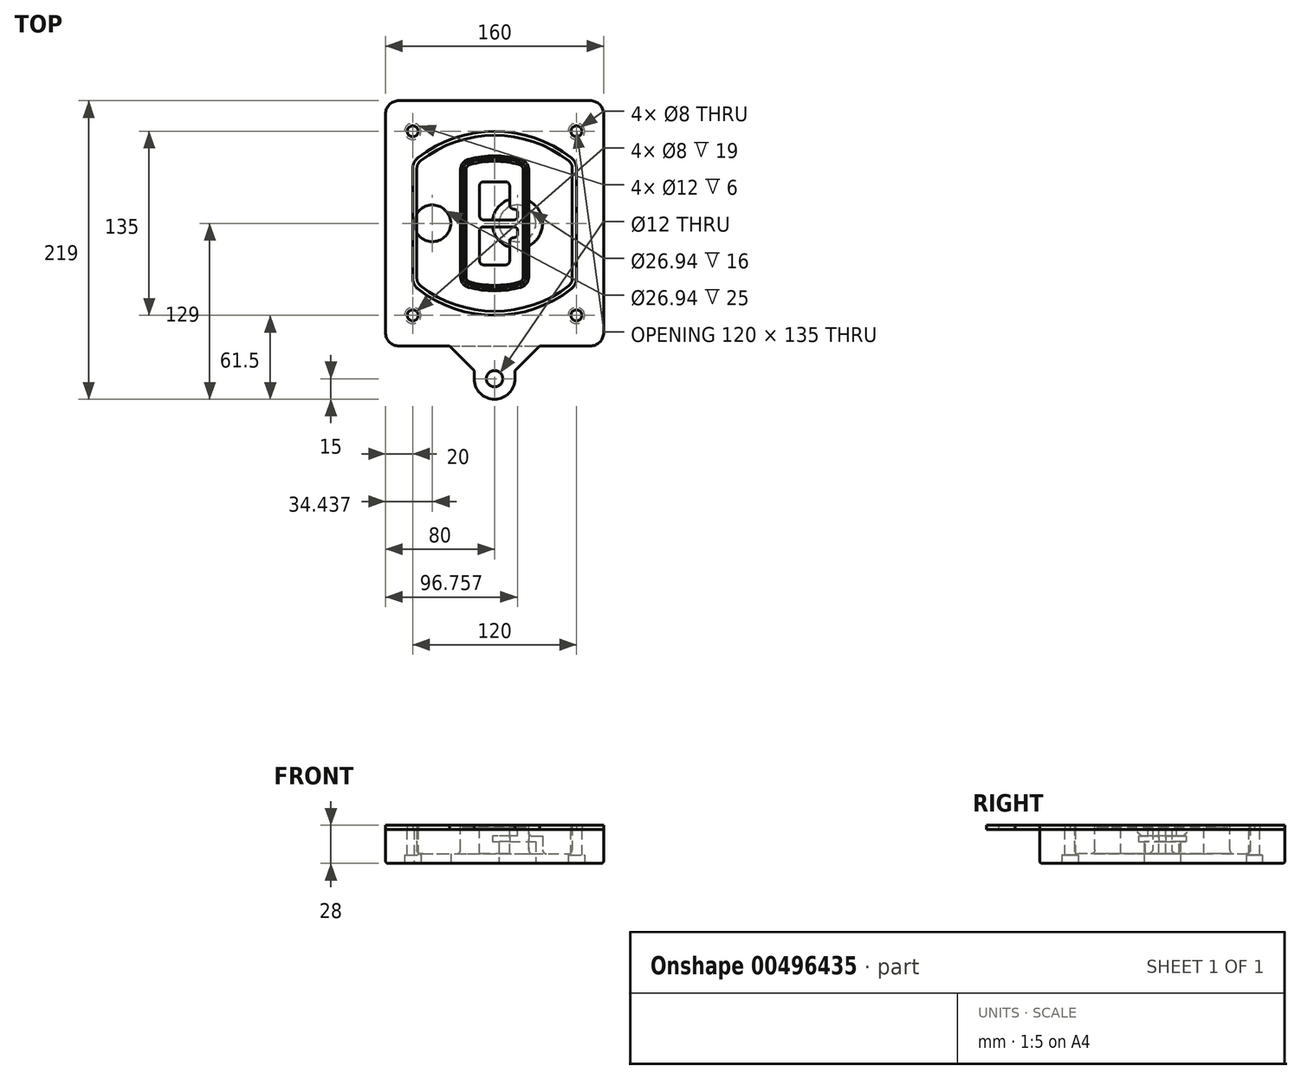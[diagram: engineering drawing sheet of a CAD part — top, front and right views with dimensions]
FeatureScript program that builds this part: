
annotation { "Feature Type Name" : "Feature", "Feature Type Description" : "" }
export const myFeature = defineFeature(function(context is Context, id is Id, definition is map)
    precondition{}
    {
        {
            var Q0;
            Q0=qCreatedBy(makeId("Top.planeOp"),FACE);
            var sketch = newSketch(context, id + "F0", { "sketchPlane" : qUnion([Q0])});
            skPoint(sketch, "E0.rect.middle", {"position": v(0, 0) * mm});
            skLineSegment(sketch, "E1.bottom", {"start": v(-70, -90) * mm, "end": v(70, -90) * mm});
            skLineSegment(sketch, "E1.top", {"start": v(-70, 90) * mm, "end": v(70, 90) * mm});
            skLineSegment(sketch, "E1.left", {"start": v(-80, -80) * mm, "end": v(-80, 80) * mm});
            skLineSegment(sketch, "E1.right", {"start": v(80, -80) * mm, "end": v(80, 80) * mm});
            skLineSegment(sketch, "E2", {"start": v(-80, 90) * mm, "end": v(80, -90) * mm, "construction": true});
            skLineSegment(sketch, "E3", {"start": v(80, 90) * mm, "end": v(-80, -90) * mm, "construction": true});
            skCircle(sketch, "E4", {"center": v(-60, 67.5) * mm, "radius": 4 * mm});
            skCircle(sketch, "E5", {"center": v(60, 67.5) * mm, "radius": 4 * mm});
            skCircle(sketch, "E6", {"center": v(60, -67.5) * mm, "radius": 4 * mm});
            skCircle(sketch, "E7", {"center": v(-60, -67.5) * mm, "radius": 4 * mm});
            skLineSegment(sketch, "E8", {"start": v(-60, 67.5) * mm, "end": v(60, 67.5) * mm, "construction": true});
            skLineSegment(sketch, "E9", {"start": v(60, 67.5) * mm, "end": v(60, -67.5) * mm, "construction": true});
            skLineSegment(sketch, "E10", {"start": v(60, -67.5) * mm, "end": v(-60, -67.5) * mm, "construction": true});
            skLineSegment(sketch, "E11", {"start": v(-60, -67.5) * mm, "end": v(-60, 67.5) * mm, "construction": true});
            skLineSegment(sketch, "E12", {"start": v(-60, 40.3) * mm, "end": v(-60, -40.3) * mm});
            skLineSegment(sketch, "E13", {"start": v(60, 40.3) * mm, "end": v(60, -40.3) * mm});
            skArc(sketch, "E14", {"start": v(56.15, 48.18) * mm, "mid": v(0, 67.5) * mm, "end": v(-56.15, 48.18) * mm});
            skArc(sketch, "E15", {"start": v(-56.15, -48.18) * mm, "mid": v(0, -67.5) * mm, "end": v(56.15, -48.18) * mm});
            skLineSegment(sketch, "E16", {"start": v(-60, 0) * mm, "end": v(60, 0) * mm, "construction": true});
            skPoint(sketch, "E17.visualSharp", {"position": v(-60, -45) * mm});
            skArc(sketch, "E17.filletArc", {"start": v(-60, -40.3) * mm, "mid": v(-58.99, -44.68) * mm, "end": v(-56.15, -48.18) * mm});
            skPoint(sketch, "E18.visualSharp", {"position": v(-60, 45) * mm});
            skArc(sketch, "E18.filletArc", {"start": v(-56.15, 48.18) * mm, "mid": v(-58.99, 44.68) * mm, "end": v(-60, 40.3) * mm});
            skPoint(sketch, "E19.visualSharp", {"position": v(60, 45) * mm});
            skArc(sketch, "E19.filletArc", {"start": v(60, 40.3) * mm, "mid": v(58.99, 44.68) * mm, "end": v(56.15, 48.18) * mm});
            skPoint(sketch, "E20.visualSharp", {"position": v(60, -45) * mm});
            skArc(sketch, "E20.filletArc", {"start": v(56.15, -48.18) * mm, "mid": v(58.99, -44.68) * mm, "end": v(60, -40.3) * mm});
            skPoint(sketch, "E21.visualSharp", {"position": v(-80, 90) * mm});
            skArc(sketch, "E21.filletArc", {"start": v(-70, 90) * mm, "mid": v(-77.07, 87.07) * mm, "end": v(-80, 80) * mm});
            skPoint(sketch, "E22.visualSharp", {"position": v(80, 90) * mm});
            skArc(sketch, "E22.filletArc", {"start": v(80, 80) * mm, "mid": v(77.07, 87.07) * mm, "end": v(70, 90) * mm});
            skPoint(sketch, "E23.visualSharp", {"position": v(80, -90) * mm});
            skArc(sketch, "E23.filletArc", {"start": v(70, -90) * mm, "mid": v(77.07, -87.07) * mm, "end": v(80, -80) * mm});
            skPoint(sketch, "E24.visualSharp", {"position": v(-80, -90) * mm});
            skArc(sketch, "E24.filletArc", {"start": v(-80, -80) * mm, "mid": v(-77.07, -87.07) * mm, "end": v(-70, -90) * mm});
            skArc(sketch, "E25.0", {"start": v(57, 40.3) * mm, "mid": v(56.3, 43.36) * mm, "end": v(54.3, 45.81) * mm});
            skLineSegment(sketch, "E25.1", {"start": v(57, 40.3) * mm, "end": v(57, -40.3) * mm});
            skArc(sketch, "E25.2", {"start": v(54.3, -45.81) * mm, "mid": v(56.3, -43.36) * mm, "end": v(57, -40.3) * mm});
            skArc(sketch, "E25.3", {"start": v(-54.3, -45.81) * mm, "mid": v(0, -64.5) * mm, "end": v(54.3, -45.81) * mm});
            skArc(sketch, "E25.4", {"start": v(-57, -40.3) * mm, "mid": v(-56.3, -43.36) * mm, "end": v(-54.3, -45.81) * mm});
            skArc(sketch, "E25.5", {"start": v(54.3, 45.81) * mm, "mid": v(0, 64.5) * mm, "end": v(-54.3, 45.81) * mm});
            skLineSegment(sketch, "E25.6", {"start": v(-57, 40.3) * mm, "end": v(-57, -40.3) * mm});
            skArc(sketch, "E25.7", {"start": v(-54.3, 45.81) * mm, "mid": v(-56.3, 43.36) * mm, "end": v(-57, 40.3) * mm});
            skArc(sketch, "E26.0", {"start": v(-58.62, 51.33) * mm, "mid": v(-62.58, 46.43) * mm, "end": v(-64, 40.3) * mm});
            skArc(sketch, "E26.1", {"start": v(58.62, 51.33) * mm, "mid": v(0, 71.5) * mm, "end": v(-58.62, 51.33) * mm});
            skArc(sketch, "E26.2", {"start": v(64, 40.3) * mm, "mid": v(62.58, 46.43) * mm, "end": v(58.62, 51.33) * mm});
            skLineSegment(sketch, "E26.3", {"start": v(64, 40.3) * mm, "end": v(64, -40.3) * mm});
            skArc(sketch, "E26.4", {"start": v(58.62, -51.33) * mm, "mid": v(62.58, -46.43) * mm, "end": v(64, -40.3) * mm});
            skLineSegment(sketch, "E26.5", {"start": v(-64, 40.3) * mm, "end": v(-64, -40.3) * mm});
            skArc(sketch, "E26.6", {"start": v(-58.62, -51.33) * mm, "mid": v(0, -71.5) * mm, "end": v(58.62, -51.33) * mm});
            skArc(sketch, "E26.7", {"start": v(-64, -40.3) * mm, "mid": v(-62.58, -46.43) * mm, "end": v(-58.62, -51.33) * mm});
            skSolve(sketch);
        }
        {
            var Q0;
            Q0=makeQuery(id+"F0.imprint","IMPRINT",FACE,{"disambiguationData":[TD([[makeQuery(id+"F0.imprint","IMPRINT",EDGE,{"derivedFrom":sQuery(id+"F0.wireOp",EDGE,"E1.bottom")}),1.0]])]});
            var Q1;
            Q1=makeQuery(id+"F0.imprint","IMPRINT",FACE,{"disambiguationData":[TD([[makeQuery(id+"F0.imprint","IMPRINT",EDGE,{"derivedFrom":sQuery(id+"F0.wireOp",EDGE,"E12")}),1.0]])]});
            var Q2;
            Q2=makeQuery(id+"F0.imprint","IMPRINT",FACE,{"disambiguationData":[TD([[makeQuery(id+"F0.imprint","IMPRINT",EDGE,{"derivedFrom":sQuery(id+"F0.wireOp",EDGE,"E25.0")}),1.0]])]});
            var Q3;
            Q3=makeQuery(id+"F0.imprint","IMPRINT",FACE,{"disambiguationData":[TD([[makeQuery(id+"F0.imprint","IMPRINT",EDGE,{"derivedFrom":sQuery(id+"F0.wireOp",EDGE,"E12")}),-1.0]])]});
            extrude(context, id + "F1", {"entities" : qUnion([Q0, Q1, Q2, Q3]), "oppositeDirection" : true, "depth" : 25 * mm});
        }
        {
            var Q0;
            Q0=makeQuery(id+"F0.imprint","IMPRINT",FACE,{"disambiguationData":[TD([[makeQuery(id+"F0.imprint","IMPRINT",EDGE,{"derivedFrom":sQuery(id+"F0.wireOp",EDGE,"E12")}),1.0]])]});
            extrude(context, id + "F2", {"entities" : qUnion([Q0]), "operationType" : NewBodyOperationType.ADD, "depth" : 3 * mm});
        }
        {
            var Q0;
            Q0=makeQuery(id+"F0.imprint","IMPRINT",FACE,{"disambiguationData":[TD([[makeQuery(id+"F0.imprint","IMPRINT",EDGE,{"derivedFrom":sQuery(id+"F0.wireOp",EDGE,"E25.0")}),1.0]])]});
            extrude(context, id + "F3", {"entities" : qUnion([Q0]), "operationType" : NewBodyOperationType.REMOVE, "oppositeDirection" : true, "depth" : 18 * mm});
        }
        {
            var Q0;
            Q0=makeQuery(id+"F2.opExtrude","CAP_FACE",FACE,{"disambiguationData":[OSD([sQuery(id+"F0.wireOp",EDGE,"E12"),sQuery(id+"F0.wireOp",EDGE,"E13"),sQuery(id+"F0.wireOp",EDGE,"E14"),sQuery(id+"F0.wireOp",EDGE,"E15"),sQuery(id+"F0.wireOp",EDGE,"E17.filletArc"),sQuery(id+"F0.wireOp",EDGE,"E18.filletArc"),sQuery(id+"F0.wireOp",EDGE,"E19.filletArc"),sQuery(id+"F0.wireOp",EDGE,"E20.filletArc"),sQuery(id+"F0.wireOp",EDGE,"E25.0"),sQuery(id+"F0.wireOp",EDGE,"E25.1"),sQuery(id+"F0.wireOp",EDGE,"E25.2"),sQuery(id+"F0.wireOp",EDGE,"E25.3"),sQuery(id+"F0.wireOp",EDGE,"E25.4"),sQuery(id+"F0.wireOp",EDGE,"E25.5"),sQuery(id+"F0.wireOp",EDGE,"E25.6"),sQuery(id+"F0.wireOp",EDGE,"E25.7")])],"isStart":false});
            var sketch = newSketch(context, id + "F4", { "sketchPlane" : qUnion([Q0])});
            skArc(sketch, "E27.0", {"start": v(-19.08, -46.97) * mm, "mid": v(0, -49.5) * mm, "end": v(19.08, -46.97) * mm});
            skArc(sketch, "E28.0", {"start": v(19.08, 46.97) * mm, "mid": v(0, 49.5) * mm, "end": v(-19.08, 46.97) * mm});
            skLineSegment(sketch, "E29", {"start": v(-25, 39.25) * mm, "end": v(-25, -39.25) * mm});
            skLineSegment(sketch, "E30", {"start": v(25, 39.25) * mm, "end": v(25, -39.25) * mm});
            skLineSegment(sketch, "E31", {"start": v(-25, 45.1) * mm, "end": v(25, 45.1) * mm, "construction": true});
            skLineSegment(sketch, "E32", {"start": v(-25, -45.1) * mm, "end": v(25, -45.1) * mm, "construction": true});
            skPoint(sketch, "E33.visualSharp", {"position": v(-25, 45.1) * mm});
            skArc(sketch, "E33.filletArc", {"start": v(-19.08, 46.97) * mm, "mid": v(-23.35, 44.11) * mm, "end": v(-25, 39.25) * mm});
            skPoint(sketch, "E34.visualSharp", {"position": v(25, 45.1) * mm});
            skArc(sketch, "E34.filletArc", {"start": v(25, 39.25) * mm, "mid": v(23.35, 44.11) * mm, "end": v(19.08, 46.97) * mm});
            skPoint(sketch, "E35.visualSharp", {"position": v(25, -45.1) * mm});
            skArc(sketch, "E35.filletArc", {"start": v(19.08, -46.97) * mm, "mid": v(23.35, -44.11) * mm, "end": v(25, -39.25) * mm});
            skPoint(sketch, "E36.visualSharp", {"position": v(-25, -45.1) * mm});
            skArc(sketch, "E36.filletArc", {"start": v(-25, -39.25) * mm, "mid": v(-23.35, -44.11) * mm, "end": v(-19.08, -46.97) * mm});
            skArc(sketch, "E37.0", {"start": v(54.3, 45.81) * mm, "mid": v(0, 64.5) * mm, "end": v(-54.3, 45.81) * mm});
            skArc(sketch, "E37.1", {"start": v(-54.3, 45.81) * mm, "mid": v(-56.3, 43.36) * mm, "end": v(-57, 40.3) * mm});
            skLineSegment(sketch, "E37.2", {"start": v(-57, 40.3) * mm, "end": v(-57, -40.3) * mm});
            skArc(sketch, "E37.3", {"start": v(-57, -40.3) * mm, "mid": v(-56.3, -43.36) * mm, "end": v(-54.3, -45.81) * mm});
            skArc(sketch, "E37.4", {"start": v(-54.3, -45.81) * mm, "mid": v(0, -64.5) * mm, "end": v(54.3, -45.81) * mm});
            skArc(sketch, "E37.5", {"start": v(54.3, -45.81) * mm, "mid": v(56.3, -43.36) * mm, "end": v(57, -40.3) * mm});
            skLineSegment(sketch, "E37.6", {"start": v(57, 40.3) * mm, "end": v(57, -40.3) * mm});
            skArc(sketch, "E37.7", {"start": v(57, 40.3) * mm, "mid": v(56.3, 43.36) * mm, "end": v(54.3, 45.81) * mm});
            skLineSegment(sketch, "E38.0", {"start": v(23, 39.25) * mm, "end": v(23, -39.25) * mm});
            skArc(sketch, "E38.1", {"start": v(18.56, -45.04) * mm, "mid": v(21.76, -42.9) * mm, "end": v(23, -39.25) * mm});
            skArc(sketch, "E38.2", {"start": v(-18.56, -45.04) * mm, "mid": v(0, -47.5) * mm, "end": v(18.56, -45.04) * mm});
            skArc(sketch, "E38.3", {"start": v(-23, -39.25) * mm, "mid": v(-21.76, -42.9) * mm, "end": v(-18.56, -45.04) * mm});
            skLineSegment(sketch, "E38.4", {"start": v(-23, 39.25) * mm, "end": v(-23, -39.25) * mm});
            skArc(sketch, "E38.5", {"start": v(23, 39.25) * mm, "mid": v(21.76, 42.9) * mm, "end": v(18.56, 45.04) * mm});
            skArc(sketch, "E38.6", {"start": v(-18.56, 45.04) * mm, "mid": v(-21.76, 42.9) * mm, "end": v(-23, 39.25) * mm});
            skArc(sketch, "E38.7", {"start": v(18.56, 45.04) * mm, "mid": v(0, 47.5) * mm, "end": v(-18.56, 45.04) * mm});
            skArc(sketch, "E39.0", {"start": v(21, 39.25) * mm, "mid": v(20.18, 41.68) * mm, "end": v(18.04, 43.1) * mm});
            skLineSegment(sketch, "E39.1", {"start": v(21, 39.25) * mm, "end": v(21, -39.25) * mm});
            skArc(sketch, "E39.2", {"start": v(18.04, -43.1) * mm, "mid": v(20.18, -41.68) * mm, "end": v(21, -39.25) * mm});
            skArc(sketch, "E39.3", {"start": v(-18.04, -43.1) * mm, "mid": v(0, -45.5) * mm, "end": v(18.04, -43.1) * mm});
            skArc(sketch, "E39.4", {"start": v(-21, -39.25) * mm, "mid": v(-20.18, -41.68) * mm, "end": v(-18.04, -43.1) * mm});
            skArc(sketch, "E39.5", {"start": v(18.04, 43.1) * mm, "mid": v(0, 45.5) * mm, "end": v(-18.04, 43.1) * mm});
            skLineSegment(sketch, "E39.6", {"start": v(-21, 39.25) * mm, "end": v(-21, -39.25) * mm});
            skArc(sketch, "E39.7", {"start": v(-18.04, 43.1) * mm, "mid": v(-20.18, 41.68) * mm, "end": v(-21, 39.25) * mm});
            skLineSegment(sketch, "E40", {"start": v(-25, 0) * mm, "end": v(25, 0) * mm, "construction": true});
            skLineSegment(sketch, "E41", {"start": v(-11, 5.5) * mm, "end": v(-11, 27.5) * mm});
            skLineSegment(sketch, "E42", {"start": v(-8, 30.5) * mm, "end": v(8, 30.5) * mm});
            skLineSegment(sketch, "E43", {"start": v(11, 27.5) * mm, "end": v(11, 13.5) * mm});
            skLineSegment(sketch, "E44", {"start": v(14, 10.5) * mm, "end": v(14, 10.5) * mm});
            skLineSegment(sketch, "E45", {"start": v(17, 7.5) * mm, "end": v(17, 5.5) * mm});
            skLineSegment(sketch, "E46", {"start": v(14, 2.5) * mm, "end": v(-8, 2.5) * mm});
            skPoint(sketch, "E47.visualSharp", {"position": v(-11, 30.5) * mm});
            skArc(sketch, "E47.filletArc", {"start": v(-8, 30.5) * mm, "mid": v(-10.12, 29.62) * mm, "end": v(-11, 27.5) * mm});
            skPoint(sketch, "E48.visualSharp", {"position": v(11, 30.5) * mm});
            skArc(sketch, "E48.filletArc", {"start": v(11, 27.5) * mm, "mid": v(10.12, 29.62) * mm, "end": v(8, 30.5) * mm});
            skPoint(sketch, "E49.visualSharp", {"position": v(11, 10.5) * mm});
            skArc(sketch, "E49.filletArc", {"start": v(11, 13.5) * mm, "mid": v(11.88, 11.38) * mm, "end": v(14, 10.5) * mm});
            skPoint(sketch, "E50.visualSharp", {"position": v(17, 10.5) * mm});
            skArc(sketch, "E50.filletArc", {"start": v(17, 7.5) * mm, "mid": v(16.12, 9.62) * mm, "end": v(14, 10.5) * mm});
            skPoint(sketch, "E51.visualSharp", {"position": v(17, 2.5) * mm});
            skArc(sketch, "E51.filletArc", {"start": v(14, 2.5) * mm, "mid": v(16.12, 3.38) * mm, "end": v(17, 5.5) * mm});
            skPoint(sketch, "E52.visualSharp", {"position": v(-11, 2.5) * mm});
            skArc(sketch, "E52.filletArc", {"start": v(-11, 5.5) * mm, "mid": v(-10.12, 3.38) * mm, "end": v(-8, 2.5) * mm});
            skLineSegment(sketch, "E53.0.MirrorCS", {"start": v(14, -2.5) * mm, "end": v(-8, -2.5) * mm});
            skArc(sketch, "E54.0.MirrorCS", {"start": v(-11, -5.5) * mm, "mid": v(-10.12, -3.38) * mm, "end": v(-8, -2.5) * mm});
            skLineSegment(sketch, "E55.0.MirrorCS", {"start": v(-11, -5.5) * mm, "end": v(-11, -27.5) * mm});
            skArc(sketch, "E56.0.MirrorCS", {"start": v(-8, -30.5) * mm, "mid": v(-10.12, -29.62) * mm, "end": v(-11, -27.5) * mm});
            skLineSegment(sketch, "E57.0.MirrorCS", {"start": v(-8, -30.5) * mm, "end": v(8, -30.5) * mm});
            skArc(sketch, "E58.0.MirrorCS", {"start": v(11, -27.5) * mm, "mid": v(10.12, -29.62) * mm, "end": v(8, -30.5) * mm});
            skLineSegment(sketch, "E59.0.MirrorCS", {"start": v(11, -27.5) * mm, "end": v(11, -13.5) * mm});
            skArc(sketch, "E60.0.MirrorCS", {"start": v(11, -13.5) * mm, "mid": v(11.88, -11.38) * mm, "end": v(14, -10.5) * mm});
            skArc(sketch, "E61.0.MirrorCS", {"start": v(17, -7.5) * mm, "mid": v(16.12, -9.62) * mm, "end": v(14, -10.5) * mm});
            skLineSegment(sketch, "E62.0.MirrorCS", {"start": v(17, -7.5) * mm, "end": v(17, -5.5) * mm});
            skArc(sketch, "E63.0.MirrorCS", {"start": v(14, -2.5) * mm, "mid": v(16.12, -3.38) * mm, "end": v(17, -5.5) * mm});
            skSolve(sketch);
        }
        {
            var Q0;
            Q0=makeQuery(id+"F4.imprint","IMPRINT",FACE,{"disambiguationData":[TD([[makeQuery(id+"F4.imprint","IMPRINT",EDGE,{"derivedFrom":sQuery(id+"F4.wireOp",EDGE,"E27.0")}),1.0]])]});
            var Q1;
            Q1=makeQuery(id+"F4.imprint","IMPRINT",FACE,{"disambiguationData":[TD([[makeQuery(id+"F4.imprint","IMPRINT",EDGE,{"derivedFrom":sQuery(id+"F4.wireOp",EDGE,"E38.0")}),-1.0]])]});
            var Q2;
            Q2=makeQuery(id+"F4.imprint","IMPRINT",FACE,{"disambiguationData":[TD([[makeQuery(id+"F4.imprint","IMPRINT",EDGE,{"derivedFrom":sQuery(id+"F4.wireOp",EDGE,"E39.0")}),1.0]])]});
            extrude(context, id + "F5", {"entities" : qUnion([Q0, Q1, Q2]), "operationType" : NewBodyOperationType.ADD, "endBound" : BoundingType.UP_TO_NEXT, "oppositeDirection" : true, "depth" : 25 * mm});
        }
        {
            var Q0;
            Q0=makeQuery(id+"F4.imprint","IMPRINT",FACE,{"disambiguationData":[TD([[makeQuery(id+"F4.imprint","IMPRINT",EDGE,{"derivedFrom":sQuery(id+"F4.wireOp",EDGE,"E38.0")}),-1.0]])]});
            extrude(context, id + "F6", {"entities" : qUnion([Q0]), "operationType" : NewBodyOperationType.REMOVE, "oppositeDirection" : true, "depth" : 2 * mm});
        }
        {
            var Q0;
            Q0=makeQuery(id+"F1.opExtrude","CAP_FACE",FACE,{"disambiguationData":[OSD([sQuery(id+"F0.wireOp",EDGE,"E1.bottom"),sQuery(id+"F0.wireOp",EDGE,"E1.top"),sQuery(id+"F0.wireOp",EDGE,"E1.left"),sQuery(id+"F0.wireOp",EDGE,"E1.right"),sQuery(id+"F0.wireOp",EDGE,"E4"),sQuery(id+"F0.wireOp",EDGE,"E5"),sQuery(id+"F0.wireOp",EDGE,"E6"),sQuery(id+"F0.wireOp",EDGE,"E7"),sQuery(id+"F0.wireOp",EDGE,"E21.filletArc"),sQuery(id+"F0.wireOp",EDGE,"E22.filletArc"),sQuery(id+"F0.wireOp",EDGE,"E23.filletArc"),sQuery(id+"F0.wireOp",EDGE,"E24.filletArc")])],"isStart":false});
            var sketch = newSketch(context, id + "F7", { "sketchPlane" : qUnion([Q0])});
            skCircle(sketch, "E64", {"center": v(16.76, 0) * mm, "radius": 13.47 * mm});
            skCircle(sketch, "E65", {"center": v(-45.56, 0) * mm, "radius": 13.47 * mm});
            skLineSegment(sketch, "E66", {"start": v(80, 0) * mm, "end": v(-80, 0) * mm});
            skCircle(sketch, "E67", {"center": v(16.76, 0) * mm, "radius": 18.47 * mm});
            skCircle(sketch, "E68", {"center": v(60, -67.5) * mm, "radius": 6 * mm});
            skCircle(sketch, "E69", {"center": v(-60, -67.5) * mm, "radius": 6 * mm});
            skCircle(sketch, "E70", {"center": v(-60, 67.5) * mm, "radius": 6 * mm});
            skCircle(sketch, "E71", {"center": v(60, 67.5) * mm, "radius": 6 * mm});
            skSolve(sketch);
        }
        {
            var Q0;
            {var subQ1=sQuery(id+"F7.wireOp",EDGE,"E66");var subQ4=sQuery(id+"F7.wireOp",EDGE,"E64");var subQ6=makeQuery(id+"F7.imprint","INTERSECT",VERTEX,{"disambiguationData":[OD(0.0)],"derivedFrom":[subQ4,subQ1]});Q0=makeQuery(id+"F7.imprint","IMPRINT",FACE,{"disambiguationData":[TD([[makeQuery(id+"F7.imprint","IMPRINT",EDGE,{"disambiguationData":[TD([[subQ6,-1.0]])],"derivedFrom":subQ4}),-1.0]])]});}
            var Q1;
            {var subQ0=sQuery(id+"F7.wireOp",EDGE,"E66");var subQ1=sQuery(id+"F7.wireOp",EDGE,"E64");var subQ3=makeQuery(id+"F7.imprint","INTERSECT",VERTEX,{"disambiguationData":[OD(0.0)],"derivedFrom":[subQ1,subQ0]});Q1=makeQuery(id+"F7.imprint","IMPRINT",FACE,{"disambiguationData":[TD([[makeQuery(id+"F7.imprint","IMPRINT",EDGE,{"disambiguationData":[TD([[subQ3,-1.0]])],"derivedFrom":subQ1}),1.0]])]});}
            var Q2;
            {var subQ0=sQuery(id+"F7.wireOp",EDGE,"E66");var subQ1=sQuery(id+"F7.wireOp",EDGE,"E64");var subQ3=makeQuery(id+"F7.imprint","INTERSECT",VERTEX,{"disambiguationData":[OD(0.0)],"derivedFrom":[subQ1,subQ0]});Q2=makeQuery(id+"F7.imprint","IMPRINT",FACE,{"disambiguationData":[TD([[makeQuery(id+"F7.imprint","IMPRINT",EDGE,{"disambiguationData":[TD([[subQ3,1.0]])],"derivedFrom":subQ1}),1.0]])]});}
            var Q3;
            {var subQ1=sQuery(id+"F7.wireOp",EDGE,"E66");var subQ4=sQuery(id+"F7.wireOp",EDGE,"E64");var subQ6=makeQuery(id+"F7.imprint","INTERSECT",VERTEX,{"disambiguationData":[OD(0.0)],"derivedFrom":[subQ4,subQ1]});Q3=makeQuery(id+"F7.imprint","IMPRINT",FACE,{"disambiguationData":[TD([[makeQuery(id+"F7.imprint","IMPRINT",EDGE,{"disambiguationData":[TD([[subQ6,1.0]])],"derivedFrom":subQ4}),-1.0]])]});}
            extrude(context, id + "F8", {"entities" : qUnion([Q0, Q1, Q2, Q3]), "operationType" : NewBodyOperationType.ADD, "oppositeDirection" : true, "depth" : 20 * mm});
        }
        {
            var Q0;
            {var subQ0=sQuery(id+"F7.wireOp",EDGE,"E66");var subQ1=sQuery(id+"F7.wireOp",EDGE,"E64");var subQ3=makeQuery(id+"F7.imprint","INTERSECT",VERTEX,{"disambiguationData":[OD(0.0)],"derivedFrom":[subQ1,subQ0]});Q0=makeQuery(id+"F7.imprint","IMPRINT",FACE,{"disambiguationData":[TD([[makeQuery(id+"F7.imprint","IMPRINT",EDGE,{"disambiguationData":[TD([[subQ3,-1.0]])],"derivedFrom":subQ1}),1.0]])]});}
            var Q1;
            {var subQ0=sQuery(id+"F7.wireOp",EDGE,"E66");var subQ1=sQuery(id+"F7.wireOp",EDGE,"E64");var subQ3=makeQuery(id+"F7.imprint","INTERSECT",VERTEX,{"disambiguationData":[OD(0.0)],"derivedFrom":[subQ1,subQ0]});Q1=makeQuery(id+"F7.imprint","IMPRINT",FACE,{"disambiguationData":[TD([[makeQuery(id+"F7.imprint","IMPRINT",EDGE,{"disambiguationData":[TD([[subQ3,1.0]])],"derivedFrom":subQ1}),1.0]])]});}
            extrude(context, id + "F9", {"entities" : qUnion([Q0, Q1]), "operationType" : NewBodyOperationType.REMOVE, "oppositeDirection" : true, "depth" : 16 * mm});
        }
        {
            var Q0;
            {var subQ0=sQuery(id+"F7.wireOp",EDGE,"E66");var subQ1=sQuery(id+"F7.wireOp",EDGE,"E65");var subQ3=makeQuery(id+"F7.imprint","INTERSECT",VERTEX,{"disambiguationData":[OD(0.0)],"derivedFrom":[subQ1,subQ0]});Q0=makeQuery(id+"F7.imprint","IMPRINT",FACE,{"disambiguationData":[TD([[makeQuery(id+"F7.imprint","IMPRINT",EDGE,{"disambiguationData":[TD([[subQ3,-1.0]])],"derivedFrom":subQ1}),1.0]])]});}
            var Q1;
            {var subQ0=sQuery(id+"F7.wireOp",EDGE,"E66");var subQ1=sQuery(id+"F7.wireOp",EDGE,"E65");var subQ3=makeQuery(id+"F7.imprint","INTERSECT",VERTEX,{"disambiguationData":[OD(0.0)],"derivedFrom":[subQ1,subQ0]});Q1=makeQuery(id+"F7.imprint","IMPRINT",FACE,{"disambiguationData":[TD([[makeQuery(id+"F7.imprint","IMPRINT",EDGE,{"disambiguationData":[TD([[subQ3,1.0]])],"derivedFrom":subQ1}),1.0]])]});}
            extrude(context, id + "F10", {"entities" : qUnion([Q0, Q1]), "operationType" : NewBodyOperationType.REMOVE, "oppositeDirection" : true, "depth" : 25 * mm});
        }
        {
            var Q0;
            Q0=makeQuery(id+"F7.imprint","IMPRINT",FACE,{"disambiguationData":[TD([[makeQuery(id+"F7.imprint","IMPRINT",EDGE,{"derivedFrom":sQuery(id+"F7.wireOp",EDGE,"E68")}),1.0]])]});
            var Q1;
            Q1=makeQuery(id+"F7.imprint","IMPRINT",FACE,{"disambiguationData":[TD([[makeQuery(id+"F7.imprint","IMPRINT",EDGE,{"derivedFrom":makeQuery(id+"F1.opExtrude","CAP_EDGE",EDGE,{"disambiguationData":[OSD([sQuery(id+"F0.wireOp",EDGE,"E5")])],"isStart":false})}),-1.0]])]});
            var Q2;
            Q2=makeQuery(id+"F7.imprint","IMPRINT",FACE,{"disambiguationData":[TD([[makeQuery(id+"F7.imprint","IMPRINT",EDGE,{"derivedFrom":sQuery(id+"F7.wireOp",EDGE,"E69")}),1.0]])]});
            var Q3;
            Q3=makeQuery(id+"F7.imprint","IMPRINT",FACE,{"disambiguationData":[TD([[makeQuery(id+"F7.imprint","IMPRINT",EDGE,{"derivedFrom":makeQuery(id+"F1.opExtrude","CAP_EDGE",EDGE,{"disambiguationData":[OSD([sQuery(id+"F0.wireOp",EDGE,"E4")])],"isStart":false})}),-1.0]])]});
            var Q4;
            Q4=makeQuery(id+"F7.imprint","IMPRINT",FACE,{"disambiguationData":[TD([[makeQuery(id+"F7.imprint","IMPRINT",EDGE,{"derivedFrom":sQuery(id+"F7.wireOp",EDGE,"E70")}),1.0]])]});
            var Q5;
            Q5=makeQuery(id+"F7.imprint","IMPRINT",FACE,{"disambiguationData":[TD([[makeQuery(id+"F7.imprint","IMPRINT",EDGE,{"derivedFrom":makeQuery(id+"F1.opExtrude","CAP_EDGE",EDGE,{"disambiguationData":[OSD([sQuery(id+"F0.wireOp",EDGE,"E7")])],"isStart":false})}),-1.0]])]});
            var Q6;
            Q6=makeQuery(id+"F7.imprint","IMPRINT",FACE,{"disambiguationData":[TD([[makeQuery(id+"F7.imprint","IMPRINT",EDGE,{"derivedFrom":sQuery(id+"F7.wireOp",EDGE,"E71")}),1.0]])]});
            var Q7;
            Q7=makeQuery(id+"F7.imprint","IMPRINT",FACE,{"disambiguationData":[TD([[makeQuery(id+"F7.imprint","IMPRINT",EDGE,{"derivedFrom":makeQuery(id+"F1.opExtrude","CAP_EDGE",EDGE,{"disambiguationData":[OSD([sQuery(id+"F0.wireOp",EDGE,"E6")])],"isStart":false})}),-1.0]])]});
            extrude(context, id + "F11", {"entities" : qUnion([Q0, Q1, Q2, Q3, Q4, Q5, Q6, Q7]), "operationType" : NewBodyOperationType.REMOVE, "oppositeDirection" : true, "depth" : 6 * mm});
        }
        {
            var Q0;
            Q0=makeQuery(id+"F9.boolean.opBoolean","COPY",FACE,{"derivedFrom":makeQuery(id+"F9.opExtrude","CAP_FACE",FACE,{"disambiguationData":[OSD([sQuery(id+"F7.wireOp",EDGE,"E64")])],"isStart":false})});
            var sketch = newSketch(context, id + "F12", { "sketchPlane" : qUnion([Q0])});
            skArc(sketch, "E72.0", {"start": v(11, 17.55) * mm, "mid": v(2.57, 11.82) * mm, "end": v(-1.54, 2.5) * mm});
            skArc(sketch, "E72.1", {"start": v(-1.54, -2.5) * mm, "mid": v(2.57, -11.82) * mm, "end": v(11, -17.55) * mm});
            skLineSegment(sketch, "E73", {"start": v(-1.54, -2.5) * mm, "end": v(14, -2.5) * mm});
            skLineSegment(sketch, "E74.0", {"start": v(14, 2.5) * mm, "end": v(-1.54, 2.5) * mm});
            skArc(sketch, "E74.1", {"start": v(14, 2.5) * mm, "mid": v(16.12, 3.38) * mm, "end": v(17, 5.5) * mm});
            skLineSegment(sketch, "E74.2", {"start": v(17, 7.5) * mm, "end": v(17, 5.5) * mm});
            skArc(sketch, "E74.3", {"start": v(17, 7.5) * mm, "mid": v(16.12, 9.62) * mm, "end": v(14, 10.5) * mm});
            skArc(sketch, "E74.4", {"start": v(11, 13.5) * mm, "mid": v(11.88, 11.38) * mm, "end": v(14, 10.5) * mm});
            skLineSegment(sketch, "E74.5", {"start": v(11, 17.55) * mm, "end": v(11, 13.5) * mm});
            skLineSegment(sketch, "E74.7", {"start": v(14, -2.5) * mm, "end": v(-1.54, -2.5) * mm});
            skArc(sketch, "E74.8", {"start": v(14, -2.5) * mm, "mid": v(16.12, -3.38) * mm, "end": v(17, -5.5) * mm});
            skLineSegment(sketch, "E74.9", {"start": v(17, -7.5) * mm, "end": v(17, -5.5) * mm});
            skArc(sketch, "E74.10", {"start": v(17, -7.5) * mm, "mid": v(16.12, -9.62) * mm, "end": v(14, -10.5) * mm});
            skArc(sketch, "E74.11", {"start": v(11, -13.5) * mm, "mid": v(11.88, -11.38) * mm, "end": v(14, -10.5) * mm});
            skLineSegment(sketch, "E74.12", {"start": v(11, -17.55) * mm, "end": v(11, -13.5) * mm});
            skPoint(sketch, "E75.orphan", {"position": v(11, -27.5) * mm});
            skPoint(sketch, "E76.orphan", {"position": v(-8, -2.5) * mm});
            skPoint(sketch, "E77.orphan", {"position": v(-8, 2.5) * mm});
            skPoint(sketch, "E78.orphan", {"position": v(11, 27.5) * mm});
            skSolve(sketch);
        }
        {
            var Q0;
            {var subQ7=sQuery(id+"F12.wireOp",EDGE,"E72.0");var subQ14=sQuery(id+"F12.wireOp",EDGE,"E72.1");var subQ16=sQuery(id+"F12.wireOp",EDGE,"E74.1");var subQ18=sQuery(id+"F12.wireOp",EDGE,"E74.8");Q0=qUnion([makeQuery(id+"F12.imprint","IMPRINT",FACE,{"disambiguationData":[TD([[makeQuery(id+"F12.imprint","IMPRINT",EDGE,{"derivedFrom":subQ7}),1.0]])]}),makeQuery(id+"F12.imprint","IMPRINT",FACE,{"disambiguationData":[TD([[makeQuery(id+"F12.imprint","IMPRINT",EDGE,{"derivedFrom":subQ14}),1.0]])]}),makeQuery(id+"F12.imprint","IMPRINT",FACE,{"disambiguationData":[TD([[makeQuery(id+"F12.imprint","IMPRINT",EDGE,{"derivedFrom":subQ16}),1.0]])]}),makeQuery(id+"F12.imprint","IMPRINT",FACE,{"disambiguationData":[TD([[makeQuery(id+"F12.imprint","IMPRINT",EDGE,{"derivedFrom":subQ18}),-1.0]])]})]);}
            var Q1;
            Q1=makeQuery(id+"F5.boolean.opBoolean","SPLIT",FACE,{"disambiguationData":[TD([makeQuery(id+"F5.opExtrude","SWEPT_FACE",FACE,{"disambiguationData":[OSD([sQuery(id+"F4.wireOp",EDGE,"E41")])]})])],"derivedFrom":makeQuery(id+"F3.boolean.opBoolean","COPY",FACE,{"derivedFrom":makeQuery(id+"F3.opExtrude","CAP_FACE",FACE,{"disambiguationData":[OSD([sQuery(id+"F0.wireOp",EDGE,"E25.0"),sQuery(id+"F0.wireOp",EDGE,"E25.1"),sQuery(id+"F0.wireOp",EDGE,"E25.2"),sQuery(id+"F0.wireOp",EDGE,"E25.3"),sQuery(id+"F0.wireOp",EDGE,"E25.4"),sQuery(id+"F0.wireOp",EDGE,"E25.5"),sQuery(id+"F0.wireOp",EDGE,"E25.6"),sQuery(id+"F0.wireOp",EDGE,"E25.7")])],"isStart":false})})});
            extrude(context, id + "F13", {"entities" : qUnion([Q0]), "operationType" : NewBodyOperationType.REMOVE, "endBound" : BoundingType.UP_TO_SURFACE, "endBoundEntityFace" : qUnion([Q1]), "depth" : 25 * mm});
        }
        {
            var Q0;
            Q0=makeQuery(id+"F3.boolean.opBoolean","COPY",EDGE,{"derivedFrom":makeQuery(id+"F3.opExtrude","CAP_EDGE",EDGE,{"disambiguationData":[OSD([sQuery(id+"F0.wireOp",EDGE,"E25.6")])],"isStart":false})});
            var Q1;
            Q1=makeQuery(id+"F8.boolean.opBoolean","INTERSECT",EDGE,{"derivedFrom":[makeQuery(id+"F5.opExtrude","SWEPT_FACE",FACE,{"disambiguationData":[OSD([sQuery(id+"F4.wireOp",EDGE,"E30")])]}),makeQuery(id+"F8.opExtrude","CAP_FACE",FACE,{"disambiguationData":[OSD([sQuery(id+"F7.wireOp",EDGE,"E67")])],"isStart":false})]});
            var Q2;
            Q2=makeQuery(id+"F8.boolean.opBoolean","INTERSECT",EDGE,{"disambiguationData":[OD(1.0)],"derivedFrom":[makeQuery(id+"F5.opExtrude","SWEPT_FACE",FACE,{"disambiguationData":[OSD([sQuery(id+"F4.wireOp",EDGE,"E30")])]}),makeQuery(id+"F8.opExtrude","SWEPT_FACE",FACE,{"disambiguationData":[OSD([sQuery(id+"F7.wireOp",EDGE,"E67")])]})]});
            var Q3;
            {var subQ0=sQuery(id+"F4.wireOp",EDGE,"E30");Q3=makeQuery(id+"F8.boolean.opBoolean","SPLIT",EDGE,{"disambiguationData":[TD([makeQuery(id+"F5.opExtrude","SWEPT_FACE",FACE,{"disambiguationData":[OSD([sQuery(id+"F4.wireOp",EDGE,"E35.filletArc")])]})])],"derivedFrom":makeQuery(id+"F5.opExtrude","CAP_EDGE",EDGE,{"disambiguationData":[OSD([subQ0])],"isStart":false})});}
            var Q4;
            {var subQ0=sQuery(id+"F0.wireOp",EDGE,"E25.7");var subQ1=sQuery(id+"F0.wireOp",EDGE,"E25.1");var subQ2=sQuery(id+"F0.wireOp",EDGE,"E25.6");var subQ3=sQuery(id+"F0.wireOp",EDGE,"E25.5");var subQ4=sQuery(id+"F0.wireOp",EDGE,"E25.4");var subQ5=sQuery(id+"F0.wireOp",EDGE,"E25.0");var subQ6=sQuery(id+"F0.wireOp",EDGE,"E25.2");var subQ7=sQuery(id+"F0.wireOp",EDGE,"E25.3");Q4=makeQuery(id+"F8.boolean.opBoolean","INTERSECT",EDGE,{"derivedFrom":[makeQuery(id+"F5.boolean.opBoolean","SPLIT",FACE,{"disambiguationData":[TD([makeQuery(id+"F2.opExtrude","SWEPT_FACE",FACE,{"disambiguationData":[OSD([subQ5])]})])],"derivedFrom":makeQuery(id+"F3.boolean.opBoolean","COPY",FACE,{"derivedFrom":makeQuery(id+"F3.opExtrude","CAP_FACE",FACE,{"disambiguationData":[OSD([subQ5,subQ1,subQ6,subQ7,subQ4,subQ3,subQ2,subQ0])],"isStart":false})})}),makeQuery(id+"F8.opExtrude","SWEPT_FACE",FACE,{"disambiguationData":[OSD([sQuery(id+"F7.wireOp",EDGE,"E67")])]})]});}
            var Q5;
            Q5=makeQuery(id+"F8.boolean.opBoolean","INTERSECT",EDGE,{"disambiguationData":[OD(0.0)],"derivedFrom":[makeQuery(id+"F5.opExtrude","SWEPT_FACE",FACE,{"disambiguationData":[OSD([sQuery(id+"F4.wireOp",EDGE,"E30")])]}),makeQuery(id+"F8.opExtrude","SWEPT_FACE",FACE,{"disambiguationData":[OSD([sQuery(id+"F7.wireOp",EDGE,"E67")])]})]});
            fillet(context, id + "F14", {"entities" : qUnion([Q0, Q1, Q2, Q3, Q4, Q5]), "radius" : 3 * mm, "tangentPropagation" : true, "allowEdgeOverflow" : false});
        }
        {
            var Q0;
            Q0=makeQuery(id+"F1.opExtrude","CAP_EDGE",EDGE,{"disambiguationData":[OSD([sQuery(id+"F0.wireOp",EDGE,"E1.bottom")])],"isStart":false});
            fillet(context, id + "F15", {"entities" : qUnion([Q0]), "radius" : 2 * mm, "tangentPropagation" : true, "allowEdgeOverflow" : false});
        }
        {
            var Q0;
            {var subQ0=sQuery(id+"F0.wireOp",EDGE,"E21.filletArc");var subQ1=sQuery(id+"F0.wireOp",EDGE,"E7");var subQ2=sQuery(id+"F0.wireOp",EDGE,"E6");var subQ3=sQuery(id+"F0.wireOp",EDGE,"E5");var subQ4=sQuery(id+"F0.wireOp",EDGE,"E4");var subQ5=sQuery(id+"F0.wireOp",EDGE,"E22.filletArc");var subQ6=sQuery(id+"F0.wireOp",EDGE,"E1.bottom");var subQ7=sQuery(id+"F0.wireOp",EDGE,"E1.right");var subQ8=sQuery(id+"F0.wireOp",EDGE,"E1.top");var subQ9=sQuery(id+"F0.wireOp",EDGE,"E1.left");var subQ10=sQuery(id+"F0.wireOp",EDGE,"E23.filletArc");var subQ11=sQuery(id+"F0.wireOp",EDGE,"E24.filletArc");Q0=makeQuery(id+"F2.boolean.opBoolean","SPLIT",FACE,{"disambiguationData":[TD([makeQuery(id+"F1.opExtrude","SWEPT_FACE",FACE,{"disambiguationData":[OSD([subQ6])]})])],"derivedFrom":makeQuery(id+"F1.opExtrude","CAP_FACE",FACE,{"disambiguationData":[OSD([subQ6,subQ8,subQ9,subQ7,subQ4,subQ3,subQ2,subQ1,subQ0,subQ5,subQ10,subQ11])],"isStart":true})});}
            var sketch = newSketch(context, id + "F16", { "sketchPlane" : qUnion([Q0])});
            skLineSegment(sketch, "E79.0", {"start": v(-70, 90) * mm, "end": v(70, 90) * mm});
            skArc(sketch, "E79.1", {"start": v(-70, 90) * mm, "mid": v(-77.07, 87.07) * mm, "end": v(-80, 80) * mm});
            skLineSegment(sketch, "E79.2", {"start": v(-80, -80) * mm, "end": v(-80, 80) * mm});
            skArc(sketch, "E79.3", {"start": v(-80, -80) * mm, "mid": v(-77.07, -87.07) * mm, "end": v(-70, -90) * mm});
            skLineSegment(sketch, "E79.4", {"start": v(-70, -90) * mm, "end": v(70, -90) * mm});
            skArc(sketch, "E79.5", {"start": v(70, -90) * mm, "mid": v(77.07, -87.07) * mm, "end": v(80, -80) * mm});
            skLineSegment(sketch, "E79.6", {"start": v(80, -80) * mm, "end": v(80, 80) * mm});
            skArc(sketch, "E79.7", {"start": v(80, 80) * mm, "mid": v(77.07, 87.07) * mm, "end": v(70, 90) * mm});
            skArc(sketch, "E79.8", {"start": v(60, 40.3) * mm, "mid": v(58.99, 44.68) * mm, "end": v(56.15, 48.18) * mm});
            skArc(sketch, "E79.9", {"start": v(56.15, 48.18) * mm, "mid": v(0, 67.5) * mm, "end": v(-56.15, 48.18) * mm});
            skArc(sketch, "E79.10", {"start": v(-56.15, 48.18) * mm, "mid": v(-58.99, 44.68) * mm, "end": v(-60, 40.3) * mm});
            skLineSegment(sketch, "E79.11", {"start": v(-60, 40.3) * mm, "end": v(-60, -40.3) * mm});
            skArc(sketch, "E79.12", {"start": v(-60, -40.3) * mm, "mid": v(-58.99, -44.68) * mm, "end": v(-56.15, -48.18) * mm});
            skArc(sketch, "E79.13", {"start": v(-56.15, -48.18) * mm, "mid": v(0, -67.5) * mm, "end": v(56.15, -48.18) * mm});
            skLineSegment(sketch, "E79.14", {"start": v(60, 40.3) * mm, "end": v(60, -40.3) * mm});
            skArc(sketch, "E79.15", {"start": v(56.15, -48.18) * mm, "mid": v(58.99, -44.68) * mm, "end": v(60, -40.3) * mm});
            skLineSegment(sketch, "E80", {"start": v(0, 23.75) * mm, "end": v(0, 114) * mm, "construction": true});
            skLineSegment(sketch, "E81", {"start": v(-33, 90) * mm, "end": v(-15, 108) * mm});
            skLineSegment(sketch, "E82", {"start": v(-15, 108) * mm, "end": v(-15, 114) * mm});
            skLineSegment(sketch, "E83", {"start": v(15, 108) * mm, "end": v(15, 114) * mm});
            skArc(sketch, "E84", {"start": v(15, 114) * mm, "mid": v(0, 129) * mm, "end": v(-15, 114) * mm});
            skCircle(sketch, "E85", {"center": v(0, 114) * mm, "radius": 6 * mm});
            skLineSegment(sketch, "E86", {"start": v(15, 108) * mm, "end": v(33, 90) * mm});
            skLineSegment(sketch, "E87.MirrorCS", {"start": v(-15, 108) * mm, "end": v(-33, 90) * mm});
            skArc(sketch, "E88.MirrorCS", {"start": v(-15, 114) * mm, "mid": v(0, 129) * mm, "end": v(15, 114) * mm});
            skLineSegment(sketch, "E89.MirrorCS", {"start": v(33, 90) * mm, "end": v(15, 108) * mm});
            skLineSegment(sketch, "E90", {"start": v(0, 0) * mm, "end": v(111.93, 0) * mm, "construction": true});
            skLineSegment(sketch, "E91", {"start": v(0, 0) * mm, "end": v(-129.66, 0) * mm, "construction": true});
            skLineSegment(sketch, "E92.MirrorCS", {"start": v(15, -108) * mm, "end": v(33, -90) * mm});
            skLineSegment(sketch, "E93.MirrorCS", {"start": v(-15, -108) * mm, "end": v(-33, -90) * mm});
            skLineSegment(sketch, "E94.MirrorCS", {"start": v(-15, -108) * mm, "end": v(-15, -114) * mm});
            skArc(sketch, "E95.MirrorCS", {"start": v(-15, -114) * mm, "mid": v(0, -129) * mm, "end": v(15, -114) * mm});
            skLineSegment(sketch, "E96.MirrorCS", {"start": v(15, -108) * mm, "end": v(15, -114) * mm});
            skCircle(sketch, "E97.MirrorC", {"center": v(0, -114) * mm, "radius": 6 * mm});
            skLineSegment(sketch, "E98", {"start": v(0, -23.75) * mm, "end": v(0, -114) * mm, "construction": true});
            skSolve(sketch);
        }
        {
            var Q0;
            Q0=makeQuery(id+"F16.imprint","IMPRINT",FACE,{"disambiguationData":[TD([[makeQuery(id+"F16.imprint","IMPRINT",EDGE,{"derivedFrom":sQuery(id+"F16.wireOp",EDGE,"E85")}),1.0]])]});
            var Q1;
            {var subQ1=sQuery(id+"F16.wireOp",EDGE,"E79.1");Q1=makeQuery(id+"F16.imprint","IMPRINT",FACE,{"disambiguationData":[TD([[makeQuery(id+"F16.imprint","IMPRINT",EDGE,{"derivedFrom":subQ1}),1.0]])]});}
            var Q2;
            {var subQ0=sQuery(id+"F16.wireOp",EDGE,"E93.MirrorCS");Q2=makeQuery(id+"F16.imprint","IMPRINT",FACE,{"disambiguationData":[TD([[makeQuery(id+"F16.imprint","IMPRINT",EDGE,{"derivedFrom":subQ0}),-1.0]])]});}
            var Q3;
            Q3=makeQuery(id+"F2.opExtrude","CAP_FACE",FACE,{"disambiguationData":[OSD([sQuery(id+"F0.wireOp",EDGE,"E12"),sQuery(id+"F0.wireOp",EDGE,"E13"),sQuery(id+"F0.wireOp",EDGE,"E14"),sQuery(id+"F0.wireOp",EDGE,"E15"),sQuery(id+"F0.wireOp",EDGE,"E17.filletArc"),sQuery(id+"F0.wireOp",EDGE,"E18.filletArc"),sQuery(id+"F0.wireOp",EDGE,"E19.filletArc"),sQuery(id+"F0.wireOp",EDGE,"E20.filletArc"),sQuery(id+"F0.wireOp",EDGE,"E25.0"),sQuery(id+"F0.wireOp",EDGE,"E25.1"),sQuery(id+"F0.wireOp",EDGE,"E25.2"),sQuery(id+"F0.wireOp",EDGE,"E25.3"),sQuery(id+"F0.wireOp",EDGE,"E25.4"),sQuery(id+"F0.wireOp",EDGE,"E25.5"),sQuery(id+"F0.wireOp",EDGE,"E25.6"),sQuery(id+"F0.wireOp",EDGE,"E25.7")])],"isStart":false});
            extrude(context, id + "F17", {"entities" : qUnion([Q0, Q1, Q2]), "endBound" : BoundingType.UP_TO_SURFACE, "endBoundEntityFace" : qUnion([Q3]), "depth" : 25 * mm});
        }
    });
